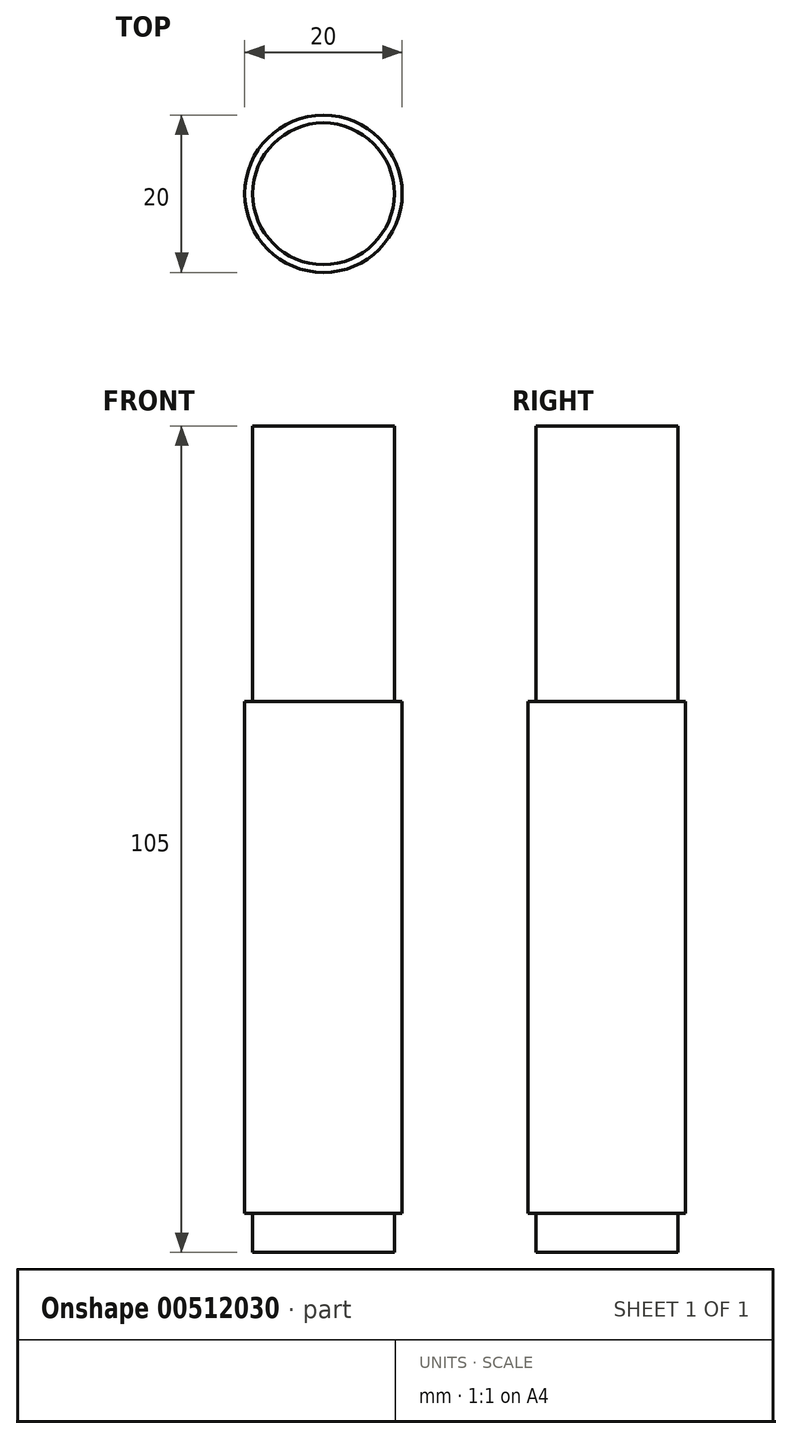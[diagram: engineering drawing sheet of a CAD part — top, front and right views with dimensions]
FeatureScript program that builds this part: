
annotation { "Feature Type Name" : "Feature", "Feature Type Description" : "" }
export const myFeature = defineFeature(function(context is Context, id is Id, definition is map)
    precondition{}
    {
        {
            var Q0;
            Q0=qCreatedBy(makeId("Top.planeOp"),FACE);
            var sketch = newSketch(context, id + "F0", { "sketchPlane" : qUnion([Q0])});
            skCircle(sketch, "E0", {"center": v(0, 0) * mm, "radius": 10 * mm});
            skCircle(sketch, "E1", {"center": v(0, 0) * mm, "radius": 9 * mm});
            skSolve(sketch);
        }
        {
            var Q0;
            Q0 = qSketchRegion(id + "F0", true);
            var Q1;
            Q1=makeQuery(id+"F0.imprint","IMPRINT",FACE,{"disambiguationData":[TD([[makeQuery(id+"F0.imprint","IMPRINT",EDGE,{"derivedFrom":sQuery(id+"F0.wireOp",EDGE,"E1")}),1.0]])]});
            extrude(context, id + "F1", {"entities" : qUnion([Q0, Q1]), "depth" : 65 * mm, "offsetDistance" : 25 * mm});
        }
        {
            var Q0;
            Q0=makeQuery(id+"F0.imprint","IMPRINT",FACE,{"disambiguationData":[TD([[makeQuery(id+"F0.imprint","IMPRINT",EDGE,{"derivedFrom":sQuery(id+"F0.wireOp",EDGE,"E1")}),1.0]])]});
            extrude(context, id + "F2", {"entities" : qUnion([Q0]), "operationType" : NewBodyOperationType.ADD, "oppositeDirection" : true, "depth" : 5 * mm, "hasSecondDirection" : true, "secondDirectionOppositeDirection" : true, "secondDirectionDepth" : -100 * mm, "offsetDistance" : 25 * mm});
        }
    });
